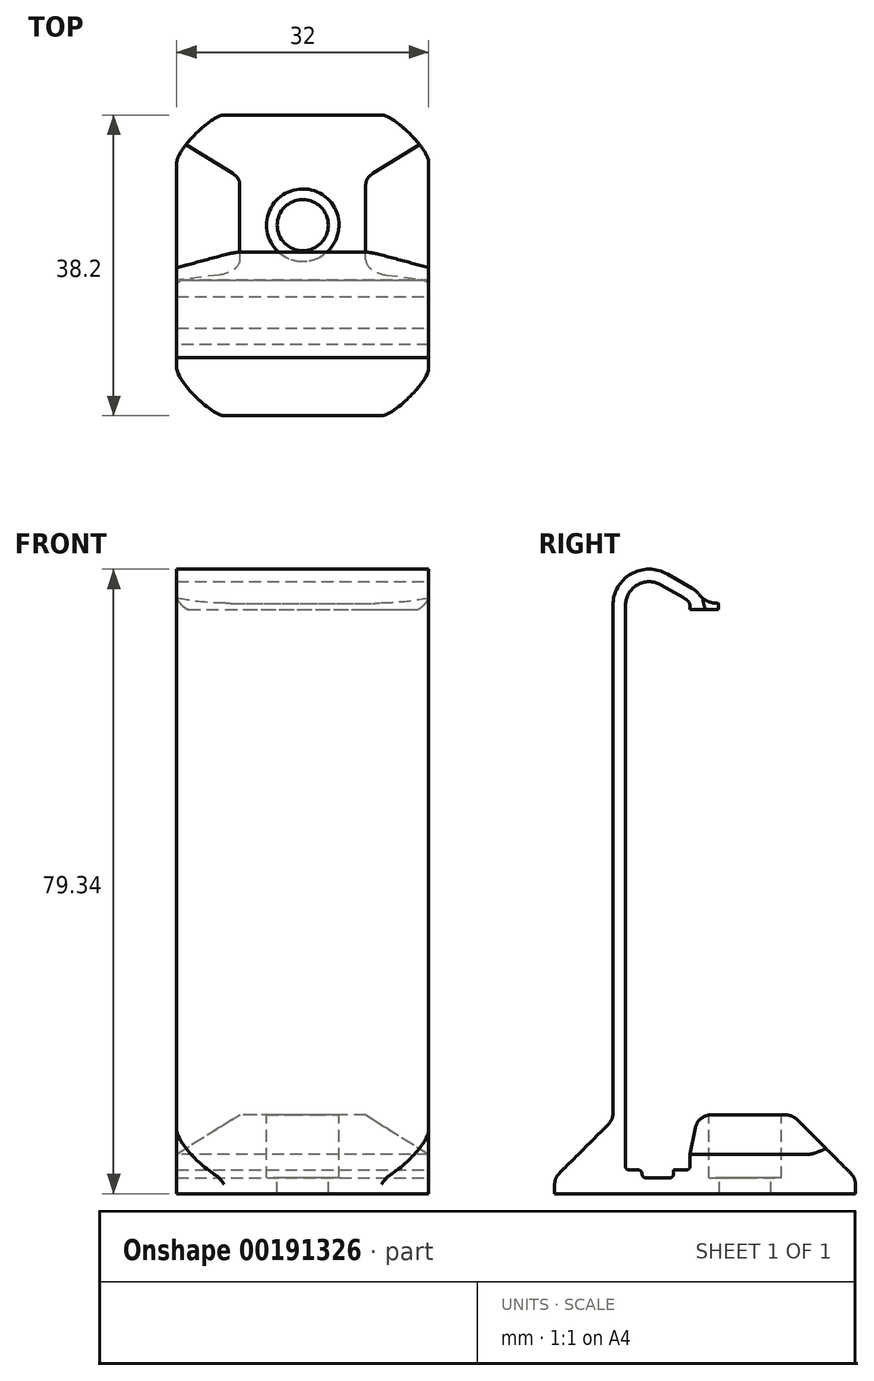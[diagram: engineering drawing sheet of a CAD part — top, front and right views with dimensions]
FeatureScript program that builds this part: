
annotation { "Feature Type Name" : "Feature", "Feature Type Description" : "" }
export const myFeature = defineFeature(function(context is Context, id is Id, definition is map)
    precondition{}
    {
        {
            var Q0;
            Q0=qCreatedBy(makeId("Right.planeOp"),FACE);
            var sketch = newSketch(context, id + "F0", { "sketchPlane" : qUnion([Q0])});
            skLineSegment(sketch, "E0.bottom", {"start": v(-4.1, 0) * mm, "end": v(4.1, 0) * mm});
            skLineSegment(sketch, "E0.top", {"start": v(-4.1, 72.2) * mm, "end": v(4.1, 72.2) * mm});
            skLineSegment(sketch, "E0.left", {"start": v(-4.1, 0) * mm, "end": v(-4.1, 72.2) * mm});
            skLineSegment(sketch, "E0.right", {"start": v(4.1, 0) * mm, "end": v(4.1, 72.2) * mm});
            skSolve(sketch);
        }
        {
            var Q0;
            Q0=qCreatedBy(makeId("Right.planeOp"),FACE);
            var sketch = newSketch(context, id + "F1", { "sketchPlane" : qUnion([Q0])});
            skLineSegment(sketch, "E1", {"start": v(-4.1, 6.4) * mm, "end": v(-5.7, 6.4) * mm});
            skLineSegment(sketch, "E2", {"start": v(-5.7, 6.4) * mm, "end": v(-13.1, -1) * mm});
            skLineSegment(sketch, "E3", {"start": v(-13.1, -1) * mm, "end": v(-13.1, -3) * mm});
            skLineSegment(sketch, "E4", {"start": v(-13.1, -3) * mm, "end": v(25.1, -3) * mm});
            skLineSegment(sketch, "E5", {"start": v(25.1, -3) * mm, "end": v(25.1, -1) * mm});
            skLineSegment(sketch, "E6", {"start": v(25.1, -1) * mm, "end": v(17.1, 7) * mm});
            skLineSegment(sketch, "E7", {"start": v(17.1, 7) * mm, "end": v(4.1, 7) * mm});
            skLineSegment(sketch, "E8", {"start": v(4.1, 7) * mm, "end": v(4.1, 0) * mm});
            skLineSegment(sketch, "E9", {"start": v(4.1, 0) * mm, "end": v(-4.1, 0) * mm});
            skLineSegment(sketch, "E10", {"start": v(-4.1, 0) * mm, "end": v(-4.1, 6.4) * mm});
            skSolve(sketch);
        }
        {
            var Q0;
            Q0 = qSketchRegion(id + "F1", true);
            extrude(context, id + "F2", {"entities" : qUnion([Q0]), "endBound" : BoundingType.SYMMETRIC, "depth" : 32 * mm});
        }
        {
            var Q0;
            Q0=makeQuery(id+"F2.opExtrude","CAP_FACE",FACE,{"disambiguationData":[OSD([sQuery(id+"F1.wireOp",EDGE,"E1"),sQuery(id+"F1.wireOp",EDGE,"E2"),sQuery(id+"F1.wireOp",EDGE,"E3"),sQuery(id+"F1.wireOp",EDGE,"E4"),sQuery(id+"F1.wireOp",EDGE,"E5"),sQuery(id+"F1.wireOp",EDGE,"E6"),sQuery(id+"F1.wireOp",EDGE,"E7"),sQuery(id+"F1.wireOp",EDGE,"E8"),sQuery(id+"F1.wireOp",EDGE,"E9"),sQuery(id+"F1.wireOp",EDGE,"E10")])],"isStart":false});
            var sketch = newSketch(context, id + "F3", { "sketchPlane" : qUnion([Q0])});
            skLineSegment(sketch, "E11", {"start": v(-5.7, 6.4) * mm, "end": v(-4.1, 6.4) * mm});
            skLineSegment(sketch, "E12", {"start": v(-4.1, 6.4) * mm, "end": v(-4.1, 71.74) * mm});
            skLineSegment(sketch, "E13", {"start": v(0.4, 74.34) * mm, "end": v(3.6, 72.49) * mm});
            skLineSegment(sketch, "E14", {"start": v(4.1, 71.62) * mm, "end": v(4.1, 71.2) * mm});
            skLineSegment(sketch, "E15", {"start": v(4.1, 71.2) * mm, "end": v(5.7, 71.2) * mm});
            skLineSegment(sketch, "E16", {"start": v(5.7, 71.2) * mm, "end": v(5.7, 71.62) * mm});
            skLineSegment(sketch, "E17", {"start": v(4.4, 73.87) * mm, "end": v(1.2, 75.72) * mm});
            skLineSegment(sketch, "E18", {"start": v(-5.7, 71.74) * mm, "end": v(-5.7, 6.4) * mm});
            skArc(sketch, "E19", {"start": v(0.4, 74.34) * mm, "mid": v(-2.6, 74.34) * mm, "end": v(-4.1, 71.74) * mm});
            skArc(sketch, "E20", {"start": v(1.2, 75.72) * mm, "mid": v(-3.4, 75.72) * mm, "end": v(-5.7, 71.74) * mm});
            skArc(sketch, "E21", {"start": v(5.7, 71.62) * mm, "mid": v(5.35, 72.92) * mm, "end": v(4.4, 73.87) * mm});
            skArc(sketch, "E22", {"start": v(4.1, 71.62) * mm, "mid": v(3.97, 72.12) * mm, "end": v(3.6, 72.49) * mm});
            skLineSegment(sketch, "E23", {"start": v(3.6, 72.49) * mm, "end": v(4.1, 72.2) * mm, "construction": true});
            skLineSegment(sketch, "E24", {"start": v(4.1, 72.2) * mm, "end": v(4.1, 71.62) * mm, "construction": true});
            skLineSegment(sketch, "E25", {"start": v(4.1, 72.2) * mm, "end": v(-4.1, 71.74) * mm, "construction": true});
            skSolve(sketch);
        }
        {
            var Q0;
            Q0 = qSketchRegion(id + "F3", true);
            var Q1;
            Q1=makeQuery(id+"F2.opExtrude","CAP_FACE",FACE,{"disambiguationData":[OSD([sQuery(id+"F1.wireOp",EDGE,"E1"),sQuery(id+"F1.wireOp",EDGE,"E2"),sQuery(id+"F1.wireOp",EDGE,"E3"),sQuery(id+"F1.wireOp",EDGE,"E4"),sQuery(id+"F1.wireOp",EDGE,"E5"),sQuery(id+"F1.wireOp",EDGE,"E6"),sQuery(id+"F1.wireOp",EDGE,"E7"),sQuery(id+"F1.wireOp",EDGE,"E8"),sQuery(id+"F1.wireOp",EDGE,"E9"),sQuery(id+"F1.wireOp",EDGE,"E10")])],"isStart":true});
            extrude(context, id + "F4", {"entities" : qUnion([Q0]), "operationType" : NewBodyOperationType.ADD, "endBound" : BoundingType.UP_TO_SURFACE, "oppositeDirection" : true, "endBoundEntityFace" : qUnion([Q1]), "depth" : 25 * mm});
        }
        {
            var Q0;
            Q0=makeQuery(id+"F4.boolean.opBoolean","MERGE",FACE,{"derivedFrom":[makeQuery(id+"F2.opExtrude","CAP_FACE",FACE,{"disambiguationData":[OSD([sQuery(id+"F1.wireOp",EDGE,"E1"),sQuery(id+"F1.wireOp",EDGE,"E2"),sQuery(id+"F1.wireOp",EDGE,"E3"),sQuery(id+"F1.wireOp",EDGE,"E4"),sQuery(id+"F1.wireOp",EDGE,"E5"),sQuery(id+"F1.wireOp",EDGE,"E6"),sQuery(id+"F1.wireOp",EDGE,"E7"),sQuery(id+"F1.wireOp",EDGE,"E8"),sQuery(id+"F1.wireOp",EDGE,"E9"),sQuery(id+"F1.wireOp",EDGE,"E10")])],"isStart":false}),makeQuery(id+"F4.opExtrude","CAP_FACE",FACE,{"disambiguationData":[OSD([sQuery(id+"F3.wireOp",EDGE,"E11"),sQuery(id+"F3.wireOp",EDGE,"E12"),sQuery(id+"F3.wireOp",EDGE,"E13"),sQuery(id+"F3.wireOp",EDGE,"E14"),sQuery(id+"F3.wireOp",EDGE,"E15"),sQuery(id+"F3.wireOp",EDGE,"E16"),sQuery(id+"F3.wireOp",EDGE,"E17"),sQuery(id+"F3.wireOp",EDGE,"E18"),sQuery(id+"F3.wireOp",EDGE,"E19"),sQuery(id+"F3.wireOp",EDGE,"E20"),sQuery(id+"F3.wireOp",EDGE,"E21"),sQuery(id+"F3.wireOp",EDGE,"E22")])],"isStart":true})]});
            var sketch = newSketch(context, id + "F5", { "sketchPlane" : qUnion([Q0])});
            skLineSegment(sketch, "E26.bottom", {"start": v(-2, 0) * mm, "end": v(2, 0) * mm});
            skLineSegment(sketch, "E26.top", {"start": v(-2, -1) * mm, "end": v(2, -1) * mm});
            skLineSegment(sketch, "E26.left", {"start": v(-2, 0) * mm, "end": v(-2, -1) * mm});
            skLineSegment(sketch, "E26.right", {"start": v(2, 0) * mm, "end": v(2, -1) * mm});
            skLineSegment(sketch, "E27", {"start": v(-4.1, 0) * mm, "end": v(-2, 0) * mm});
            skLineSegment(sketch, "E28", {"start": v(2, 0) * mm, "end": v(4.1, 0) * mm});
            skSolve(sketch);
        }
        {
            var Q0;
            Q0 = qSketchRegion(id + "F5", true);
            extrude(context, id + "F6", {"entities" : qUnion([Q0]), "operationType" : NewBodyOperationType.REMOVE, "endBound" : BoundingType.THROUGH_ALL, "oppositeDirection" : true, "depth" : 25 * mm});
        }
        {
            var Q0;
            Q0=makeQuery(id+"F2.opExtrude","SWEPT_EDGE",EDGE,{"disambiguationData":[OSD([sQuery(id+"F1.wireOp",EDGE,"E7"),sQuery(id+"F1.wireOp",EDGE,"E8")])]});
            chamfer(context, id + "F7", {"entities" : qUnion([Q0]), "chamferType" : ChamferType.TWO_OFFSETS, "width1" : 5 * mm, "oppositeDirection" : false, "width2" : 1 * mm, "tangentPropagation" : true});
        }
        {
            var Q0;
            Q0=makeQuery(id+"F2.opExtrude","SWEPT_FACE",FACE,{"disambiguationData":[OSD([sQuery(id+"F1.wireOp",EDGE,"E7")])]});
            var sketch = newSketch(context, id + "F8", { "sketchPlane" : qUnion([Q0])});
            skCircle(sketch, "E29", {"center": v(0, 11.1) * mm, "radius": 4.6 * mm});
            skLineSegment(sketch, "E30", {"start": v(0, 6.5) * mm, "end": v(0, 5.1) * mm, "construction": true});
            skLineSegment(sketch, "E31", {"start": v(0, 15.7) * mm, "end": v(0, 17.1) * mm, "construction": true});
            skSolve(sketch);
        }
        {
            var Q0;
            Q0 = qSketchRegion(id + "F8", true);
            extrude(context, id + "F9", {"entities" : qUnion([Q0]), "operationType" : NewBodyOperationType.REMOVE, "oppositeDirection" : true, "depth" : 8 * mm});
        }
        {
            var Q0;
            Q0=makeQuery(id+"F9.boolean.opBoolean","COPY",FACE,{"derivedFrom":makeQuery(id+"F9.opExtrude","CAP_FACE",FACE,{"disambiguationData":[OSD([sQuery(id+"F8.wireOp",EDGE,"E29")])],"isStart":false})});
            var sketch = newSketch(context, id + "F10", { "sketchPlane" : qUnion([Q0])});
            skCircle(sketch, "E32", {"center": v(0, 11.1) * mm, "radius": 3.25 * mm});
            skSolve(sketch);
        }
        {
            var Q0;
            Q0 = qSketchRegion(id + "F10", true);
            extrude(context, id + "F11", {"entities" : qUnion([Q0]), "operationType" : NewBodyOperationType.REMOVE, "endBound" : BoundingType.UP_TO_NEXT, "oppositeDirection" : true, "depth" : 25 * mm});
        }
        {
            var Q0;
            Q0=makeQuery(id+"F2.opExtrude","SWEPT_EDGE",EDGE,{"disambiguationData":[OSD([sQuery(id+"F1.wireOp",EDGE,"E9"),sQuery(id+"F1.wireOp",EDGE,"E10")])]});
            var Q1;
            Q1=makeQuery(id+"F2.opExtrude","SWEPT_EDGE",EDGE,{"disambiguationData":[OSD([sQuery(id+"F1.wireOp",EDGE,"E8"),sQuery(id+"F1.wireOp",EDGE,"E9")])]});
            var Q2;
            Q2=makeQuery(id+"F2.opExtrude","SWEPT_EDGE",EDGE,{"disambiguationData":[OSD([sQuery(id+"F1.wireOp",EDGE,"E7"),sQuery(id+"F1.wireOp",EDGE,"E8")])]});
            var Q3;
            Q3=makeQuery(id+"F6.boolean.opBoolean","COPY",EDGE,{"derivedFrom":makeQuery(id+"F6.opExtrude","SWEPT_EDGE",EDGE,{"disambiguationData":[OSD([sQuery(id+"F5.wireOp",EDGE,"E26.top"),sQuery(id+"F5.wireOp",EDGE,"E26.right")])]})});
            var Q4;
            Q4=makeQuery(id+"F6.boolean.opBoolean","COPY",EDGE,{"derivedFrom":makeQuery(id+"F6.opExtrude","SWEPT_EDGE",EDGE,{"disambiguationData":[OSD([sQuery(id+"F5.wireOp",EDGE,"E26.top"),sQuery(id+"F5.wireOp",EDGE,"E26.left")])]})});
            var Q5;
            Q5=makeQuery(id+"F6.boolean.opBoolean","COPY",EDGE,{"derivedFrom":makeQuery(id+"F6.opExtrude","SWEPT_EDGE",EDGE,{"disambiguationData":[OSD([sQuery(id+"F5.wireOp",EDGE,"E26.bottom"),sQuery(id+"F5.wireOp",EDGE,"E26.right"),sQuery(id+"F5.wireOp",EDGE,"E28")])]})});
            var Q6;
            Q6=makeQuery(id+"F6.boolean.opBoolean","COPY",EDGE,{"derivedFrom":makeQuery(id+"F6.opExtrude","SWEPT_EDGE",EDGE,{"disambiguationData":[OSD([sQuery(id+"F5.wireOp",EDGE,"E26.bottom"),sQuery(id+"F5.wireOp",EDGE,"E26.left"),sQuery(id+"F5.wireOp",EDGE,"E27")])]})});
            fillet(context, id + "F12", {"entities" : qUnion([Q0, Q1, Q2, Q3, Q4, Q5, Q6]), "radius" : .5 * mm, "tangentPropagation" : true, "allowEdgeOverflow" : false});
        }
        {
            var Q0;
            Q0=makeQuery(id+"F2.opExtrude","SWEPT_EDGE",EDGE,{"disambiguationData":[OSD([sQuery(id+"F1.wireOp",EDGE,"E5"),sQuery(id+"F1.wireOp",EDGE,"E6")])]});
            var Q1;
            Q1=makeQuery(id+"F2.opExtrude","SWEPT_EDGE",EDGE,{"disambiguationData":[OSD([sQuery(id+"F1.wireOp",EDGE,"E6"),sQuery(id+"F1.wireOp",EDGE,"E7")])]});
            var Q2;
            {var subQ0=sQuery(id+"F1.wireOp",EDGE,"E2");Q2=makeQuery(id+"F4.boolean.opBoolean","MERGE",EDGE,{"derivedFrom":[makeQuery(id+"F2.opExtrude","SWEPT_EDGE",EDGE,{"disambiguationData":[OSD([sQuery(id+"F1.wireOp",EDGE,"E1"),subQ0])]}),makeQuery(id+"F4.opExtrude","SWEPT_EDGE",EDGE,{"disambiguationData":[OSD([subQ0,sQuery(id+"F3.wireOp",EDGE,"E11"),sQuery(id+"F3.wireOp",EDGE,"E18")])]})]});}
            var Q3;
            Q3=makeQuery(id+"F2.opExtrude","SWEPT_EDGE",EDGE,{"disambiguationData":[OSD([sQuery(id+"F1.wireOp",EDGE,"E2"),sQuery(id+"F1.wireOp",EDGE,"E3")])]});
            var Q4;
            {var subQ0=sQuery(id+"F1.wireOp",EDGE,"E7");Q4=makeQuery(id+"F7.opChamfer","BLEND_EDGE",EDGE,{"blendedFrom":[makeQuery(id+"F2.opExtrude","SWEPT_EDGE",EDGE,{"disambiguationData":[OSD([subQ0,sQuery(id+"F1.wireOp",EDGE,"E8")])]}),makeQuery(id+"F2.opExtrude","SWEPT_FACE",FACE,{"disambiguationData":[OSD([subQ0])]})],"blendedInto":[makeQuery(id+"F2.opExtrude","SWEPT_FACE",FACE,{"disambiguationData":[OSD([subQ0])]})]});}
            fillet(context, id + "F13", {"entities" : qUnion([Q0, Q1, Q2, Q3, Q4]), "radius" : 2 * mm, "tangentPropagation" : true, "allowEdgeOverflow" : false});
        }
        {
            var Q0;
            Q0=makeQuery(id+"F2.opExtrude","CAP_EDGE",EDGE,{"disambiguationData":[OSD([sQuery(id+"F1.wireOp",EDGE,"E3")])],"isStart":false});
            var Q1;
            Q1=makeQuery(id+"F2.opExtrude","CAP_EDGE",EDGE,{"disambiguationData":[OSD([sQuery(id+"F1.wireOp",EDGE,"E5")])],"isStart":false});
            var Q2;
            Q2=makeQuery(id+"F2.opExtrude","CAP_EDGE",EDGE,{"disambiguationData":[OSD([sQuery(id+"F1.wireOp",EDGE,"E5")])],"isStart":true});
            var Q3;
            Q3=makeQuery(id+"F2.opExtrude","CAP_EDGE",EDGE,{"disambiguationData":[OSD([sQuery(id+"F1.wireOp",EDGE,"E3")])],"isStart":true});
            fillet(context, id + "F14", {"entities" : qUnion([Q0, Q1, Q2, Q3]), "radius" : 6 * mm, "rho" : .2, "crossSection" : FilletCrossSection.CONIC, "allowEdgeOverflow" : false});
        }
        {
            var Q0;
            Q0=makeQuery(id+"F2.opExtrude","CAP_EDGE",EDGE,{"disambiguationData":[OSD([sQuery(id+"F1.wireOp",EDGE,"E7")])],"isStart":true});
            var Q1;
            Q1=makeQuery(id+"F2.opExtrude","CAP_EDGE",EDGE,{"disambiguationData":[OSD([sQuery(id+"F1.wireOp",EDGE,"E7")])],"isStart":false});
            chamfer(context, id + "F15", {"entities" : qUnion([Q0, Q1]), "chamferType" : ChamferType.TWO_OFFSETS, "width1" : 8 * mm, "oppositeDirection" : false, "width2" : 5 * mm});
        }
        {
            var Q0;
            Q0=makeQuery(id+"F4.opExtrude","SWEPT_FACE",FACE,{"disambiguationData":[OSD([sQuery(id+"F3.wireOp",EDGE,"E15")])]});
            var sketch = newSketch(context, id + "F16", { "sketchPlane" : qUnion([Q0])});
            skLineSegment(sketch, "E33", {"start": v(-16, -5.7) * mm, "end": v(-9.8, -7.36) * mm});
            skLineSegment(sketch, "E34", {"start": v(-7.22, -7.7) * mm, "end": v(7.22, -7.7) * mm});
            skLineSegment(sketch, "E35", {"start": v(9.8, -7.36) * mm, "end": v(16, -5.7) * mm});
            skPoint(sketch, "E36.visualSharp", {"position": v(8.54, -7.7) * mm});
            skArc(sketch, "E36.filletArc", {"start": v(7.22, -7.7) * mm, "mid": v(8.52, -7.61) * mm, "end": v(9.8, -7.36) * mm});
            skPoint(sketch, "E37.visualSharp", {"position": v(-8.54, -7.7) * mm});
            skArc(sketch, "E37.filletArc", {"start": v(-9.8, -7.36) * mm, "mid": v(-8.52, -7.61) * mm, "end": v(-7.22, -7.7) * mm});
            skLineSegment(sketch, "E38", {"start": v(16, -5.7) * mm, "end": v(16, -4.1) * mm});
            skLineSegment(sketch, "E39", {"start": v(16, -4.1) * mm, "end": v(-16, -4.1) * mm});
            skLineSegment(sketch, "E40", {"start": v(-16, -4.1) * mm, "end": v(-16, -5.7) * mm});
            skSolve(sketch);
        }
        {
            var Q0;
            Q0 = qSketchRegion(id + "F16", true);
            extrude(context, id + "F17", {"entities" : qUnion([Q0]), "operationType" : NewBodyOperationType.ADD, "oppositeDirection" : true, "depth" : .8 * mm});
        }
        {
            var Q0;
            Q0=makeQuery(id+"F17.boolean.opBoolean","INTERSECT",EDGE,{"derivedFrom":[makeQuery(id+"F4.opExtrude","SWEPT_FACE",FACE,{"disambiguationData":[OSD([sQuery(id+"F3.wireOp",EDGE,"E21")])]}),makeQuery(id+"F17.opExtrude","CAP_FACE",FACE,{"disambiguationData":[OSD([sQuery(id+"F16.wireOp",EDGE,"E33"),sQuery(id+"F16.wireOp",EDGE,"E34"),sQuery(id+"F16.wireOp",EDGE,"E35"),sQuery(id+"F16.wireOp",EDGE,"E36.filletArc"),sQuery(id+"F16.wireOp",EDGE,"E37.filletArc"),sQuery(id+"F16.wireOp",EDGE,"E38"),sQuery(id+"F16.wireOp",EDGE,"E39"),sQuery(id+"F16.wireOp",EDGE,"E40")])],"isStart":false})]});
            fillet(context, id + "F18", {"entities" : qUnion([Q0]), "radius" : 3 * mm, "tangentPropagation" : true, "allowEdgeOverflow" : false});
        }
        {
            var Q0;
            Q0=makeQuery(id+"F4.opExtrude","CAP_EDGE",EDGE,{"disambiguationData":[OSD([sQuery(id+"F3.wireOp",EDGE,"E15")])],"isStart":true});
            var Q1;
            Q1=makeQuery(id+"F4.opExtrude","CAP_EDGE",EDGE,{"disambiguationData":[OSD([sQuery(id+"F3.wireOp",EDGE,"E15")])],"isStart":false});
            fillet(context, id + "F19", {"entities" : qUnion([Q0, Q1]), "radius" : 1.5 * mm, "tangentPropagation" : true, "rho" : .2, "crossSection" : FilletCrossSection.CONIC, "allowEdgeOverflow" : false});
        }
    });
